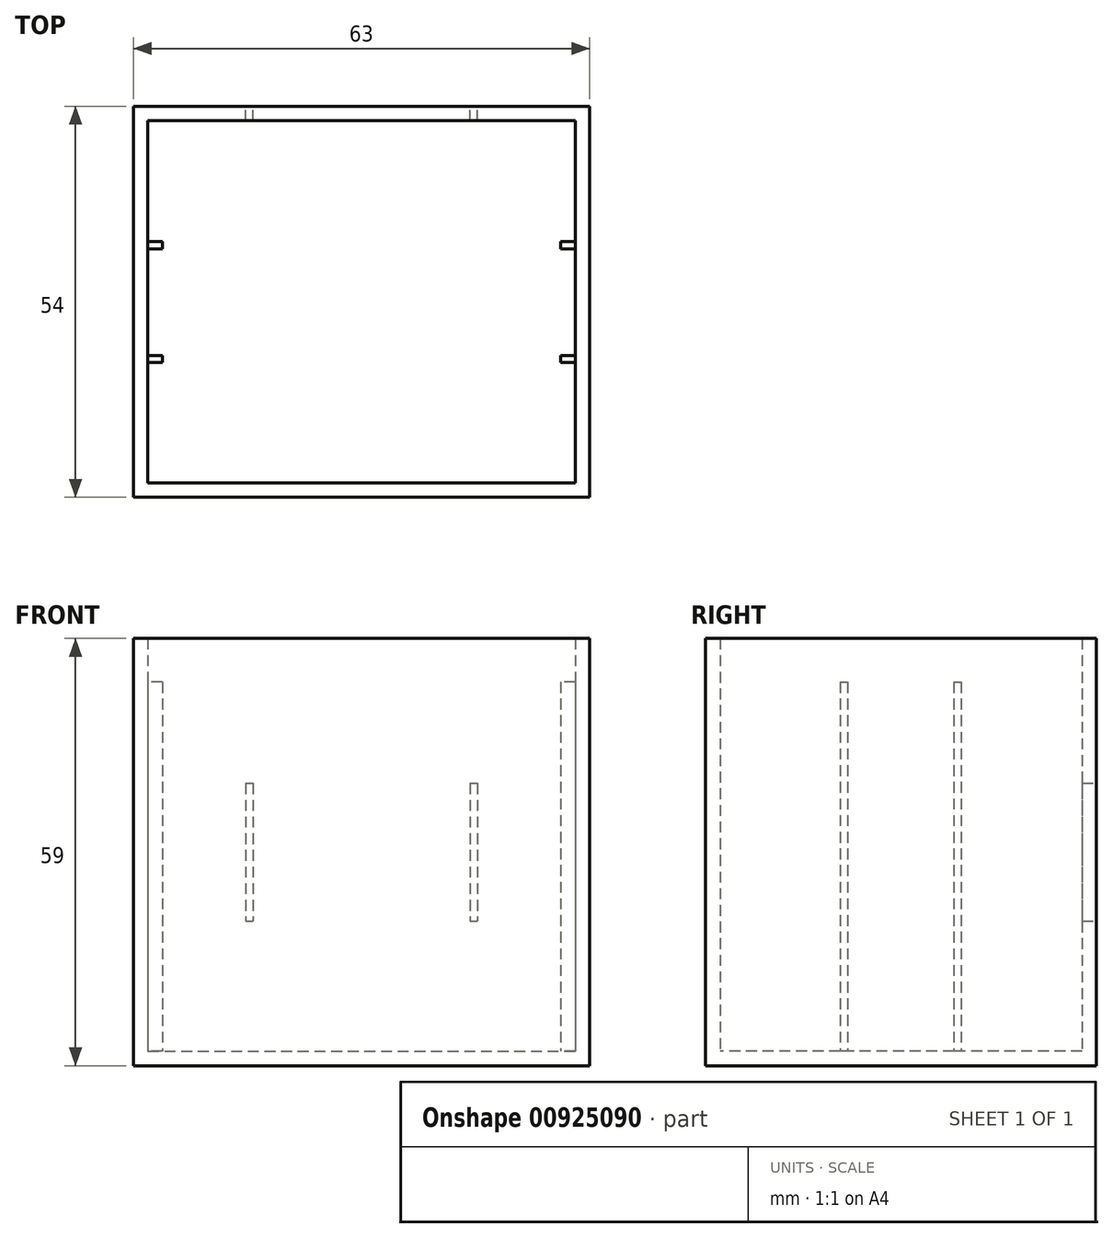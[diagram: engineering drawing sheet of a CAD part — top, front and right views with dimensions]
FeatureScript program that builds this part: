
annotation { "Feature Type Name" : "Feature", "Feature Type Description" : "" }
export const myFeature = defineFeature(function(context is Context, id is Id, definition is map)
    precondition{}
    {
        {
            var Q0;
            Q0=qCreatedBy(makeId("Top.planeOp"),FACE);
            var sketch = newSketch(context, id + "F0", { "sketchPlane" : qUnion([Q0])});
            skLineSegment(sketch, "E0.bottom", {"start": v(-839.63, -691) * mm, "end": v(-776.63, -691) * mm});
            skLineSegment(sketch, "E0.top", {"start": v(-839.63, -745) * mm, "end": v(-776.63, -745) * mm});
            skLineSegment(sketch, "E0.left", {"start": v(-839.63, -691) * mm, "end": v(-839.63, -745) * mm});
            skLineSegment(sketch, "E0.right", {"start": v(-776.63, -691) * mm, "end": v(-776.63, -745) * mm});
            skLineSegment(sketch, "E1.bottom", {"start": v(-837.63, -693) * mm, "end": v(-778.63, -693) * mm});
            skLineSegment(sketch, "E1.top", {"start": v(-837.63, -743) * mm, "end": v(-778.63, -743) * mm});
            skLineSegment(sketch, "E1.left", {"start": v(-837.63, -693) * mm, "end": v(-837.63, -743) * mm});
            skLineSegment(sketch, "E1.right", {"start": v(-778.63, -693) * mm, "end": v(-778.63, -743) * mm});
            skSolve(sketch);
        }
        {
            var Q0;
            Q0=makeQuery(id+"F0.imprint","IMPRINT",FACE,{"disambiguationData":[TD([[makeQuery(id+"F0.imprint","IMPRINT",EDGE,{"derivedFrom":sQuery(id+"F0.wireOp",EDGE,"E0.bottom")}),-1.0]])]});
            extrude(context, id + "F1", {"entities" : qUnion([Q0]), "depth" : 59 * mm, "offsetDistance" : 25.4 * mm});
        }
        {
            var Q0;
            Q0=makeQuery(id+"F0.imprint","IMPRINT",FACE,{"disambiguationData":[TD([[makeQuery(id+"F0.imprint","IMPRINT",EDGE,{"derivedFrom":sQuery(id+"F0.wireOp",EDGE,"E1.bottom")}),-1.0]])]});
            extrude(context, id + "F2", {"entities" : qUnion([Q0]), "operationType" : NewBodyOperationType.ADD, "depth" : 2 * mm, "offsetDistance" : 25 * mm});
        }
        {
            var Q0;
            Q0=makeQuery(id+"F1.opExtrude","SWEPT_FACE",FACE,{"disambiguationData":[OSD([sQuery(id+"F0.wireOp",EDGE,"E1.left")])]});
            var sketch = newSketch(context, id + "F3", { "sketchPlane" : qUnion([Q0])});
            skLineSegment(sketch, "E2.bottom", {"start": v(-726.4, 53) * mm, "end": v(-725.4, 53) * mm});
            skLineSegment(sketch, "E2.top", {"start": v(-725.4, 2) * mm, "end": v(-726.4, 2) * mm});
            skLineSegment(sketch, "E2.left", {"start": v(-725.4, 53) * mm, "end": v(-725.4, 2) * mm});
            skLineSegment(sketch, "E2.right", {"start": v(-726.4, 53) * mm, "end": v(-726.4, 2) * mm});
            skLineSegment(sketch, "E3.bottom", {"start": v(-710.7, 53) * mm, "end": v(-709.7, 53) * mm});
            skLineSegment(sketch, "E3.top", {"start": v(-709.7, 2) * mm, "end": v(-710.7, 2) * mm});
            skLineSegment(sketch, "E3.left", {"start": v(-710.7, 53) * mm, "end": v(-710.7, 2) * mm});
            skLineSegment(sketch, "E3.right", {"start": v(-709.7, 53) * mm, "end": v(-709.7, 2) * mm});
            skSolve(sketch);
        }
        {
            var Q0;
            Q0=makeQuery(id+"F3.imprint","IMPRINT",FACE,{"disambiguationData":[TD([[makeQuery(id+"F3.imprint","IMPRINT",EDGE,{"derivedFrom":sQuery(id+"F3.wireOp",EDGE,"E3.bottom")}),-1.0]])]});
            var Q1;
            Q1=makeQuery(id+"F3.imprint","IMPRINT",FACE,{"disambiguationData":[TD([[makeQuery(id+"F3.imprint","IMPRINT",EDGE,{"derivedFrom":sQuery(id+"F3.wireOp",EDGE,"E2.bottom")}),-1.0]])]});
            extrude(context, id + "F4", {"entities" : qUnion([Q0, Q1]), "operationType" : NewBodyOperationType.ADD, "depth" : 2 * mm, "offsetDistance" : 25 * mm});
        }
        {
            var Q0;
            Q0=makeQuery(id+"F3.imprint","IMPRINT",FACE,{"disambiguationData":[TD([[makeQuery(id+"F3.imprint","IMPRINT",EDGE,{"derivedFrom":sQuery(id+"F3.wireOp",EDGE,"E3.bottom")}),-1.0]])]});
            var Q1;
            Q1=makeQuery(id+"F3.imprint","IMPRINT",FACE,{"disambiguationData":[TD([[makeQuery(id+"F3.imprint","IMPRINT",EDGE,{"derivedFrom":sQuery(id+"F3.wireOp",EDGE,"E2.bottom")}),-1.0]])]});
            extrude(context, id + "F5", {"entities" : qUnion([Q0, Q1]), "operationType" : NewBodyOperationType.ADD, "depth" : 59 * mm, "offsetDistance" : 25 * mm, "hasSecondDirection" : true, "secondDirectionOppositeDirection" : false, "secondDirectionDepth" : 57 * mm});
        }
        {
            var Q0;
            Q0=makeQuery(id+"F1.opExtrude","SWEPT_FACE",FACE,{"disambiguationData":[OSD([sQuery(id+"F0.wireOp",EDGE,"E0.bottom")])]});
            var sketch = newSketch(context, id + "F6", { "sketchPlane" : qUnion([Q0])});
            skLineSegment(sketch, "E4.bottom", {"start": v(824.13, 39) * mm, "end": v(823.13, 39) * mm});
            skLineSegment(sketch, "E4.top", {"start": v(824.13, 20) * mm, "end": v(823.13, 20) * mm});
            skLineSegment(sketch, "E4.left", {"start": v(824.13, 39) * mm, "end": v(824.13, 20) * mm});
            skLineSegment(sketch, "E4.right", {"start": v(823.13, 39) * mm, "end": v(823.13, 20) * mm});
            skLineSegment(sketch, "E5.bottom", {"start": v(793.13, 39) * mm, "end": v(792.13, 39) * mm});
            skLineSegment(sketch, "E5.top", {"start": v(793.13, 20) * mm, "end": v(792.13, 20) * mm});
            skLineSegment(sketch, "E5.left", {"start": v(793.13, 39) * mm, "end": v(793.13, 20) * mm});
            skLineSegment(sketch, "E5.right", {"start": v(792.13, 39) * mm, "end": v(792.13, 20) * mm});
            skLineSegment(sketch, "E6", {"start": v(792.13, 29.5) * mm, "end": v(776.63, 29.5) * mm, "construction": true});
            skLineSegment(sketch, "E7", {"start": v(824.13, 29.5) * mm, "end": v(839.63, 29.5) * mm, "construction": true});
            skSolve(sketch);
        }
        {
            var Q0;
            Q0=makeQuery(id+"F6.imprint","IMPRINT",FACE,{"disambiguationData":[TD([[makeQuery(id+"F6.imprint","IMPRINT",EDGE,{"derivedFrom":sQuery(id+"F6.wireOp",EDGE,"E4.bottom")}),1.0]])]});
            var Q1;
            Q1=makeQuery(id+"F6.imprint","IMPRINT",FACE,{"disambiguationData":[TD([[makeQuery(id+"F6.imprint","IMPRINT",EDGE,{"derivedFrom":sQuery(id+"F6.wireOp",EDGE,"E5.bottom")}),1.0]])]});
            extrude(context, id + "F7", {"entities" : qUnion([Q0, Q1]), "operationType" : NewBodyOperationType.REMOVE, "oppositeDirection" : true, "depth" : 3 * mm, "offsetDistance" : 25 * mm});
        }
    });
